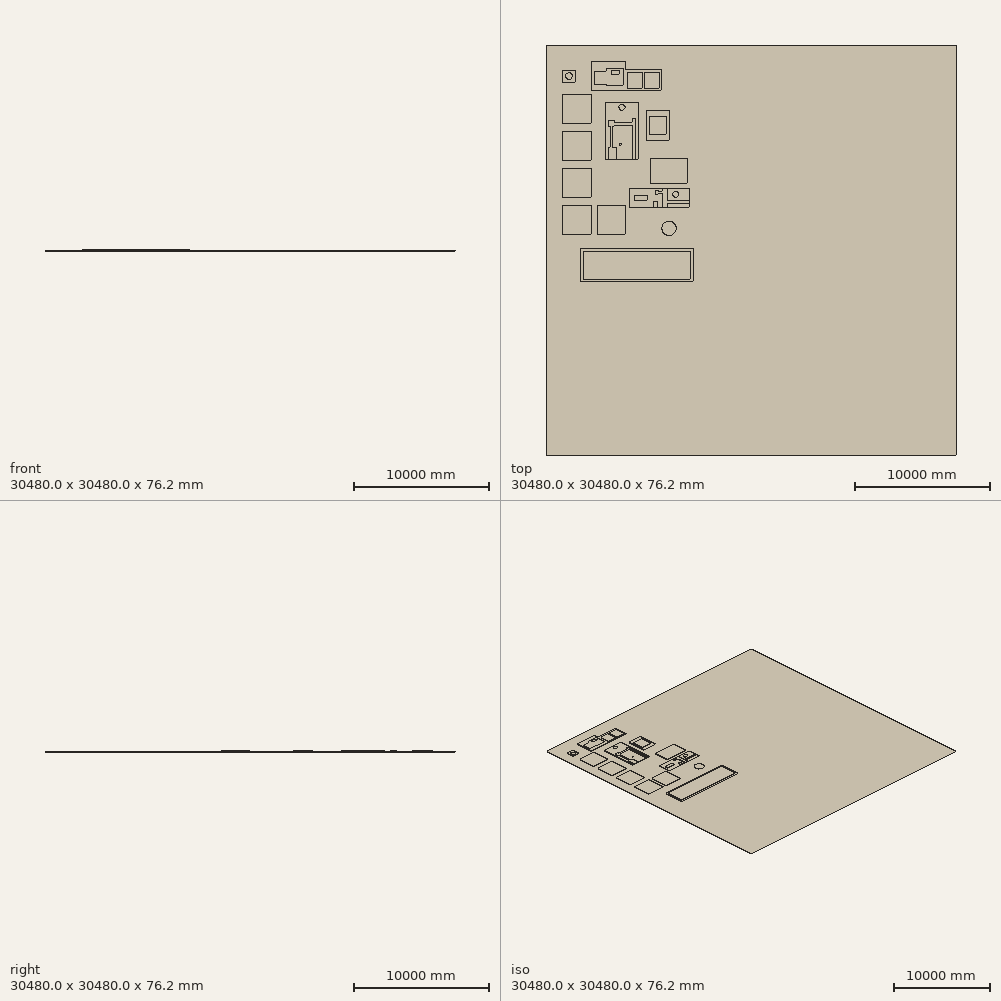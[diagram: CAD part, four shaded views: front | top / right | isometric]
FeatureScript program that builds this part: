
annotation { "Feature Type Name" : "Feature", "Feature Type Description" : "" }
export const myFeature = defineFeature(function(context is Context, id is Id, definition is map)
    precondition{}
    {
        {
            var Q0;
            Q0=qCreatedBy(makeId("Top.planeOp"),FACE);
            var sketch = newSketch(context, id + "F0", { "sketchPlane" : qUnion([Q0])});
            skLineSegment(sketch, "E0.bottom", {"start": v(15240, 15240) * mm, "end": v(-15240, 15240) * mm});
            skLineSegment(sketch, "E0.top", {"start": v(15240, -15240) * mm, "end": v(-15240, -15240) * mm});
            skLineSegment(sketch, "E0.left", {"start": v(15240, 15240) * mm, "end": v(15240, -15240) * mm});
            skLineSegment(sketch, "E0.right", {"start": v(-15240, 15240) * mm, "end": v(-15240, -15240) * mm});
            skPoint(sketch, "E0.middle", {"position": v(0, 0) * mm});
            skSolve(sketch);
        }
        {
            var Q0;
            Q0=qSketchRegion(id+"F0",true);
            extrude(context, id + "F1", {"entities" : qUnion([Q0]), "depth" : 25.4 * mm, "offsetDistance" : 25.4 * mm});
        }
        {
            var Q0;
            Q0=makeQuery(id+"F1.opExtrude","CAP_FACE",FACE,{"disambiguationData":[OSD([sQuery(id+"F0.wireOp",EDGE,"E0.bottom"),sQuery(id+"F0.wireOp",EDGE,"E0.top"),sQuery(id+"F0.wireOp",EDGE,"E0.left"),sQuery(id+"F0.wireOp",EDGE,"E0.right")])],"isStart":false});
            var sketch = newSketch(context, id + "F2", { "sketchPlane" : qUnion([Q0])});
            skLineSegment(sketch, "E1.bottom", {"start": v(-11887.2, 13462) * mm, "end": v(-6705.6, 13462) * mm});
            skLineSegment(sketch, "E1.top", {"start": v(-11887.2, 11887.2) * mm, "end": v(-6705.6, 11887.2) * mm});
            skLineSegment(sketch, "E1.left", {"start": v(-11887.2, 13462) * mm, "end": v(-11887.2, 11887.2) * mm});
            skLineSegment(sketch, "E1.right", {"start": v(-6705.6, 13462) * mm, "end": v(-6705.6, 11887.2) * mm});
            skLineSegment(sketch, "E2.bottom", {"start": v(-14020.8, 13411.2) * mm, "end": v(-13106.4, 13411.2) * mm});
            skLineSegment(sketch, "E2.top", {"start": v(-14020.8, 12496.8) * mm, "end": v(-13106.4, 12496.8) * mm});
            skLineSegment(sketch, "E2.left", {"start": v(-14020.8, 13411.2) * mm, "end": v(-14020.8, 12496.8) * mm});
            skLineSegment(sketch, "E2.right", {"start": v(-13106.4, 13411.2) * mm, "end": v(-13106.4, 12496.8) * mm});
            skCircle(sketch, "E3", {"center": v(-13563.6, 12954) * mm, "radius": 254 * mm});
            skLineSegment(sketch, "E4.bottom", {"start": v(-9046.45, 4622.8) * mm, "end": v(-4601.45, 4622.8) * mm});
            skLineSegment(sketch, "E4.top", {"start": v(-9046.45, 3175) * mm, "end": v(-4601.45, 3175) * mm});
            skLineSegment(sketch, "E4.left", {"start": v(-9046.45, 4622.8) * mm, "end": v(-9046.45, 3175) * mm});
            skLineSegment(sketch, "E4.right", {"start": v(-4601.45, 4622.8) * mm, "end": v(-4601.45, 3175) * mm});
            skCircle(sketch, "E5", {"center": v(-6125.45, 1637.27) * mm, "radius": 533.4 * mm});
            skLineSegment(sketch, "E6.bottom", {"start": v(-12678.65, 113.27) * mm, "end": v(-4296.65, 113.27) * mm});
            skLineSegment(sketch, "E6.top", {"start": v(-12678.65, -2325.13) * mm, "end": v(-4296.65, -2325.13) * mm});
            skLineSegment(sketch, "E6.left", {"start": v(-12678.65, 113.27) * mm, "end": v(-12678.65, -2325.13) * mm});
            skLineSegment(sketch, "E6.right", {"start": v(-4296.65, 113.27) * mm, "end": v(-4296.65, -2325.13) * mm});
            skLineSegment(sketch, "E7.bottom", {"start": v(-11887.2, 13462) * mm, "end": v(-9347.2, 13462) * mm});
            skLineSegment(sketch, "E7.top", {"start": v(-11887.2, 14020.8) * mm, "end": v(-9347.2, 14020.8) * mm});
            skLineSegment(sketch, "E7.left", {"start": v(-11887.2, 13462) * mm, "end": v(-11887.2, 14020.8) * mm});
            skLineSegment(sketch, "E7.right", {"start": v(-9347.2, 13462) * mm, "end": v(-9347.2, 14020.8) * mm});
            skLineSegment(sketch, "E8.bottom", {"start": v(-7797.8, 10414) * mm, "end": v(-6096, 10414) * mm});
            skLineSegment(sketch, "E8.top", {"start": v(-7797.8, 8153.4) * mm, "end": v(-6096, 8153.4) * mm});
            skLineSegment(sketch, "E8.left", {"start": v(-7797.8, 10414) * mm, "end": v(-7797.8, 8153.4) * mm});
            skLineSegment(sketch, "E8.right", {"start": v(-6096, 10414) * mm, "end": v(-6096, 8153.4) * mm});
            skLineSegment(sketch, "E9.bottom", {"start": v(-10845.8, 11023.6) * mm, "end": v(-8407.4, 11023.6) * mm});
            skLineSegment(sketch, "E9.top", {"start": v(-10845.8, 6756.4) * mm, "end": v(-8407.4, 6756.4) * mm});
            skLineSegment(sketch, "E9.left", {"start": v(-10845.8, 11023.6) * mm, "end": v(-10845.8, 6756.4) * mm});
            skLineSegment(sketch, "E9.right", {"start": v(-8407.4, 11023.6) * mm, "end": v(-8407.4, 6756.4) * mm});
            skLineSegment(sketch, "E10.bottom", {"start": v(-14020.8, 9448.8) * mm, "end": v(-14020.8, 11582.4) * mm});
            skLineSegment(sketch, "E10.top", {"start": v(-11887.2, 9448.8) * mm, "end": v(-11887.2, 11582.4) * mm});
            skLineSegment(sketch, "E10.left", {"start": v(-14020.8, 9448.8) * mm, "end": v(-11887.2, 9448.8) * mm});
            skLineSegment(sketch, "E10.right", {"start": v(-14020.8, 11582.4) * mm, "end": v(-11887.2, 11582.4) * mm});
            skLineSegment(sketch, "E11.bottom", {"start": v(-14020.8, 8839.2) * mm, "end": v(-11887.2, 8839.2) * mm});
            skLineSegment(sketch, "E11.top", {"start": v(-14020.8, 6705.6) * mm, "end": v(-11887.2, 6705.6) * mm});
            skLineSegment(sketch, "E11.left", {"start": v(-14020.8, 8839.2) * mm, "end": v(-14020.8, 6705.6) * mm});
            skLineSegment(sketch, "E11.right", {"start": v(-11887.2, 8839.2) * mm, "end": v(-11887.2, 6705.6) * mm});
            skLineSegment(sketch, "E12.bottom", {"start": v(-14020.8, 6096) * mm, "end": v(-11887.2, 6096) * mm});
            skLineSegment(sketch, "E12.top", {"start": v(-14020.8, 3962.4) * mm, "end": v(-11887.2, 3962.4) * mm});
            skLineSegment(sketch, "E12.left", {"start": v(-14020.8, 6096) * mm, "end": v(-14020.8, 3962.4) * mm});
            skLineSegment(sketch, "E12.right", {"start": v(-11887.2, 6096) * mm, "end": v(-11887.2, 3962.4) * mm});
            skLineSegment(sketch, "E13.bottom", {"start": v(-14020.8, 3352.8) * mm, "end": v(-11887.2, 3352.8) * mm});
            skLineSegment(sketch, "E13.top", {"start": v(-14020.8, 1219.2) * mm, "end": v(-11887.2, 1219.2) * mm});
            skLineSegment(sketch, "E13.left", {"start": v(-14020.8, 3352.8) * mm, "end": v(-14020.8, 1219.2) * mm});
            skLineSegment(sketch, "E13.right", {"start": v(-11887.2, 3352.8) * mm, "end": v(-11887.2, 1219.2) * mm});
            skLineSegment(sketch, "E14.bottom", {"start": v(-11463.98, 3338.27) * mm, "end": v(-9330.38, 3338.27) * mm});
            skLineSegment(sketch, "E14.top", {"start": v(-11463.98, 1204.67) * mm, "end": v(-9330.38, 1204.67) * mm});
            skLineSegment(sketch, "E14.left", {"start": v(-11463.98, 3338.27) * mm, "end": v(-11463.98, 1204.67) * mm});
            skLineSegment(sketch, "E14.right", {"start": v(-9330.38, 3338.27) * mm, "end": v(-9330.38, 1204.67) * mm});
            skLineSegment(sketch, "E15.bottom", {"start": v(-7489.64, 6810.85) * mm, "end": v(-4746.44, 6810.85) * mm});
            skLineSegment(sketch, "E15.top", {"start": v(-7489.64, 4982.05) * mm, "end": v(-4746.44, 4982.05) * mm});
            skLineSegment(sketch, "E15.left", {"start": v(-7489.64, 6810.85) * mm, "end": v(-7489.64, 4982.05) * mm});
            skLineSegment(sketch, "E15.right", {"start": v(-4746.44, 6810.85) * mm, "end": v(-4746.44, 4982.05) * mm});
            skSolve(sketch);
        }
        {
            var Q0;
            Q0=qSketchRegion(id+"F2",true);
            extrude(context, id + "F3", {"entities" : qUnion([Q0]), "operationType" : NewBodyOperationType.ADD, "depth" : 25.4 * mm, "offsetDistance" : 25.4 * mm});
        }
        {
            var Q0;
            Q0=makeQuery(id+"F3.opExtrude","CAP_FACE",FACE,{"disambiguationData":[OSD([sQuery(id+"F2.wireOp",EDGE,"E1.bottom"),sQuery(id+"F2.wireOp",EDGE,"E1.top"),sQuery(id+"F2.wireOp",EDGE,"E1.left"),sQuery(id+"F2.wireOp",EDGE,"E1.right"),sQuery(id+"F2.wireOp",EDGE,"biDbiMLD-SDf2-hi3V-axfX-EiKsOqyBmbyk.top"),sQuery(id+"F2.wireOp",EDGE,"biDbiMLD-SDf2-hi3V-axfX-EiKsOqyBmbyk.left"),sQuery(id+"F2.wireOp",EDGE,"biDbiMLD-SDf2-hi3V-axfX-EiKsOqyBmbyk.right")])],"isStart":false});
            var sketch = newSketch(context, id + "F4", { "sketchPlane" : qUnion([Q0])});
            skPoint(sketch, "E16.centerSnap0", {"position": v(-6705.6, 12674.6) * mm});
            skLineSegment(sketch, "E17.bottom", {"start": v(-8716.25, 4064) * mm, "end": v(-7751.05, 4064) * mm});
            skLineSegment(sketch, "E17.top", {"start": v(-8716.25, 3683) * mm, "end": v(-7751.05, 3683) * mm});
            skLineSegment(sketch, "E17.left", {"start": v(-8716.25, 4064) * mm, "end": v(-8716.25, 3683) * mm});
            skLineSegment(sketch, "E17.right", {"start": v(-7751.05, 4064) * mm, "end": v(-7751.05, 3683) * mm});
            skLineSegment(sketch, "E18.bottom", {"start": v(-7141.45, 4445) * mm, "end": v(-6938.25, 4445) * mm});
            skLineSegment(sketch, "E18.top", {"start": v(-7141.45, 4165.6) * mm, "end": v(-6938.25, 4165.6) * mm});
            skLineSegment(sketch, "E18.left", {"start": v(-7141.45, 4445) * mm, "end": v(-7141.45, 4165.6) * mm});
            skLineSegment(sketch, "E18.right", {"start": v(-6938.25, 4445) * mm, "end": v(-6938.25, 4165.6) * mm});
            skLineSegment(sketch, "E19.bottom", {"start": v(-6633.45, 4622.8) * mm, "end": v(-6252.45, 4622.8) * mm});
            skLineSegment(sketch, "E19.top", {"start": v(-6633.45, 3175) * mm, "end": v(-6252.45, 3175) * mm});
            skLineSegment(sketch, "E19.left", {"start": v(-6633.45, 4622.8) * mm, "end": v(-6633.45, 3175) * mm});
            skLineSegment(sketch, "E19.right", {"start": v(-6252.45, 4622.8) * mm, "end": v(-6252.45, 3175) * mm});
            skLineSegment(sketch, "E20.bottom", {"start": v(-6252.45, 3530.6) * mm, "end": v(-4601.45, 3530.6) * mm});
            skLineSegment(sketch, "E20.top", {"start": v(-6252.45, 3683) * mm, "end": v(-4601.45, 3683) * mm});
            skLineSegment(sketch, "E20.left", {"start": v(-6252.45, 3530.6) * mm, "end": v(-6252.45, 3683) * mm});
            skLineSegment(sketch, "E20.right", {"start": v(-4601.45, 3530.6) * mm, "end": v(-4601.45, 3683) * mm});
            skLineSegment(sketch, "E21.bottom", {"start": v(-6633.45, 4267.2) * mm, "end": v(-6938.25, 4267.2) * mm});
            skLineSegment(sketch, "E21.top", {"start": v(-6633.45, 4368.8) * mm, "end": v(-6938.25, 4368.8) * mm});
            skLineSegment(sketch, "E21.left", {"start": v(-6633.45, 4267.2) * mm, "end": v(-6633.45, 4368.8) * mm});
            skLineSegment(sketch, "E21.right", {"start": v(-6938.25, 4267.2) * mm, "end": v(-6938.25, 4368.8) * mm});
            skCircle(sketch, "E22", {"center": v(-5617.45, 4165.6) * mm, "radius": 228.6 * mm});
            skLineSegment(sketch, "E23.bottom", {"start": v(-7293.85, 3175) * mm, "end": v(-6989.05, 3175) * mm});
            skLineSegment(sketch, "E23.top", {"start": v(-7293.85, 3657.6) * mm, "end": v(-6989.05, 3657.6) * mm});
            skLineSegment(sketch, "E23.left", {"start": v(-7293.85, 3175) * mm, "end": v(-7293.85, 3657.6) * mm});
            skLineSegment(sketch, "E23.right", {"start": v(-6989.05, 3175) * mm, "end": v(-6989.05, 3657.6) * mm});
            skLineSegment(sketch, "E24.bottom", {"start": v(-11684, 13081) * mm, "end": v(-10769.6, 13081) * mm});
            skLineSegment(sketch, "E24.top", {"start": v(-11684, 12573) * mm, "end": v(-10769.6, 12573) * mm});
            skLineSegment(sketch, "E24.left", {"start": v(-11684, 13081) * mm, "end": v(-11684, 12573) * mm});
            skLineSegment(sketch, "E24.right", {"start": v(-10769.6, 13081) * mm, "end": v(-10769.6, 12573) * mm});
            skLineSegment(sketch, "E25.bottom", {"start": v(-10769.6, 13538.2) * mm, "end": v(-9499.6, 13538.2) * mm});
            skLineSegment(sketch, "E25.top", {"start": v(-10769.6, 12268.2) * mm, "end": v(-9499.6, 12268.2) * mm});
            skLineSegment(sketch, "E25.left", {"start": v(-10769.6, 13538.2) * mm, "end": v(-10769.6, 12268.2) * mm});
            skLineSegment(sketch, "E25.right", {"start": v(-9499.6, 13538.2) * mm, "end": v(-9499.6, 12268.2) * mm});
            skLineSegment(sketch, "E26.bottom", {"start": v(-10439.4, 13411.2) * mm, "end": v(-9804.4, 13411.2) * mm});
            skLineSegment(sketch, "E26.top", {"start": v(-10439.4, 13106.4) * mm, "end": v(-9804.4, 13106.4) * mm});
            skLineSegment(sketch, "E26.left", {"start": v(-10439.4, 13411.2) * mm, "end": v(-10439.4, 13106.4) * mm});
            skLineSegment(sketch, "E26.right", {"start": v(-9804.4, 13411.2) * mm, "end": v(-9804.4, 13106.4) * mm});
            skLineSegment(sketch, "E27.bottom", {"start": v(-11684, 13284.2) * mm, "end": v(-10769.6, 13284.2) * mm});
            skLineSegment(sketch, "E27.top", {"start": v(-11684, 12369.8) * mm, "end": v(-10769.6, 12369.8) * mm});
            skLineSegment(sketch, "E27.left", {"start": v(-11684, 13284.2) * mm, "end": v(-11684, 12369.8) * mm});
            skLineSegment(sketch, "E27.right", {"start": v(-10769.6, 13284.2) * mm, "end": v(-10769.6, 12369.8) * mm});
            skLineSegment(sketch, "E28.bottom", {"start": v(-12475.45, -89.93) * mm, "end": v(-4499.85, -89.93) * mm});
            skLineSegment(sketch, "E28.top", {"start": v(-12475.45, -2121.93) * mm, "end": v(-4499.85, -2121.93) * mm});
            skLineSegment(sketch, "E28.left", {"start": v(-12475.45, -89.93) * mm, "end": v(-12475.45, -2121.93) * mm});
            skLineSegment(sketch, "E28.right", {"start": v(-4499.85, -89.93) * mm, "end": v(-4499.85, -2121.93) * mm});
            skLineSegment(sketch, "E29.bottom", {"start": v(-9220.2, 13208) * mm, "end": v(-8077.2, 13208) * mm});
            skLineSegment(sketch, "E29.top", {"start": v(-9220.2, 12065) * mm, "end": v(-8077.2, 12065) * mm});
            skLineSegment(sketch, "E29.left", {"start": v(-9220.2, 13208) * mm, "end": v(-9220.2, 12065) * mm});
            skLineSegment(sketch, "E29.right", {"start": v(-8077.2, 13208) * mm, "end": v(-8077.2, 12065) * mm});
            skLineSegment(sketch, "E30.bottom", {"start": v(-7975.6, 13208) * mm, "end": v(-6832.6, 13208) * mm});
            skLineSegment(sketch, "E30.top", {"start": v(-7975.6, 12065) * mm, "end": v(-6832.6, 12065) * mm});
            skLineSegment(sketch, "E30.left", {"start": v(-7975.6, 13208) * mm, "end": v(-7975.6, 12065) * mm});
            skLineSegment(sketch, "E30.right", {"start": v(-6832.6, 13208) * mm, "end": v(-6832.6, 12065) * mm});
            skLineSegment(sketch, "E31.bottom", {"start": v(-7556.5, 9982.2) * mm, "end": v(-6337.3, 9982.2) * mm});
            skLineSegment(sketch, "E31.top", {"start": v(-7556.5, 8610.6) * mm, "end": v(-6337.3, 8610.6) * mm});
            skLineSegment(sketch, "E31.left", {"start": v(-7556.5, 9982.2) * mm, "end": v(-7556.5, 8610.6) * mm});
            skLineSegment(sketch, "E31.right", {"start": v(-6337.3, 9982.2) * mm, "end": v(-6337.3, 8610.6) * mm});
            skLineSegment(sketch, "E32.bottom", {"start": v(-10632.44, 6756.4) * mm, "end": v(-10022.84, 6756.4) * mm});
            skLineSegment(sketch, "E32.top", {"start": v(-10632.44, 7670.8) * mm, "end": v(-10022.84, 7670.8) * mm});
            skLineSegment(sketch, "E32.left", {"start": v(-10632.44, 6756.4) * mm, "end": v(-10632.44, 7670.8) * mm});
            skLineSegment(sketch, "E32.right", {"start": v(-10022.84, 6756.4) * mm, "end": v(-10022.84, 7670.8) * mm});
            skPoint(sketch, "E33.oppositeSnap0", {"position": v(-10327.64, 7670.8) * mm});
            skLineSegment(sketch, "E33.bottom", {"start": v(-10449.56, 7670.8) * mm, "end": v(-10327.64, 7670.8) * mm});
            skLineSegment(sketch, "E33.top", {"start": v(-10449.56, 9194.8) * mm, "end": v(-10327.64, 9194.8) * mm});
            skLineSegment(sketch, "E33.left", {"start": v(-10449.56, 7670.8) * mm, "end": v(-10449.56, 9194.8) * mm});
            skLineSegment(sketch, "E33.right", {"start": v(-10327.64, 7670.8) * mm, "end": v(-10327.64, 9194.8) * mm});
            skLineSegment(sketch, "E34.bottom", {"start": v(-10632.44, 9194.8) * mm, "end": v(-10175.24, 9194.8) * mm});
            skLineSegment(sketch, "E34.top", {"start": v(-10632.44, 9652) * mm, "end": v(-10175.24, 9652) * mm});
            skLineSegment(sketch, "E34.left", {"start": v(-10632.44, 9194.8) * mm, "end": v(-10632.44, 9652) * mm});
            skLineSegment(sketch, "E34.right", {"start": v(-10175.24, 9194.8) * mm, "end": v(-10175.24, 9652) * mm});
            skLineSegment(sketch, "E35.bottom", {"start": v(-8834.12, 9804.4) * mm, "end": v(-8620.76, 9804.4) * mm});
            skLineSegment(sketch, "E35.top", {"start": v(-8834.12, 6756.4) * mm, "end": v(-8620.76, 6756.4) * mm});
            skLineSegment(sketch, "E35.left", {"start": v(-8834.12, 9804.4) * mm, "end": v(-8834.12, 6756.4) * mm});
            skLineSegment(sketch, "E35.right", {"start": v(-8620.76, 9804.4) * mm, "end": v(-8620.76, 6756.4) * mm});
            skCircle(sketch, "E36", {"center": v(-9626.6, 10642.6) * mm, "radius": 228.6 * mm});
            skLineSegment(sketch, "E37.bottom", {"start": v(-10175.24, 9499.6) * mm, "end": v(-8834.12, 9499.6) * mm});
            skLineSegment(sketch, "E37.top", {"start": v(-10175.24, 9316.72) * mm, "end": v(-8834.12, 9316.72) * mm});
            skLineSegment(sketch, "E37.left", {"start": v(-10175.24, 9499.6) * mm, "end": v(-10175.24, 9316.72) * mm});
            skLineSegment(sketch, "E37.right", {"start": v(-8834.12, 9499.6) * mm, "end": v(-8834.12, 9316.72) * mm});
            skLineSegment(sketch, "E38.bottom", {"start": v(-9794.24, 7975.6) * mm, "end": v(-9641.84, 7975.6) * mm});
            skLineSegment(sketch, "E38.top", {"start": v(-9794.24, 7823.2) * mm, "end": v(-9641.84, 7823.2) * mm});
            skLineSegment(sketch, "E38.left", {"start": v(-9794.24, 7975.6) * mm, "end": v(-9794.24, 7823.2) * mm});
            skLineSegment(sketch, "E38.right", {"start": v(-9641.84, 7975.6) * mm, "end": v(-9641.84, 7823.2) * mm});
            skSolve(sketch);
        }
        {
            var Q0;
            Q0=qSketchRegion(id+"F4",true);
            extrude(context, id + "F5", {"entities" : qUnion([Q0]), "operationType" : NewBodyOperationType.ADD, "depth" : 25.4 * mm, "offsetDistance" : 25.4 * mm});
        }
    });
